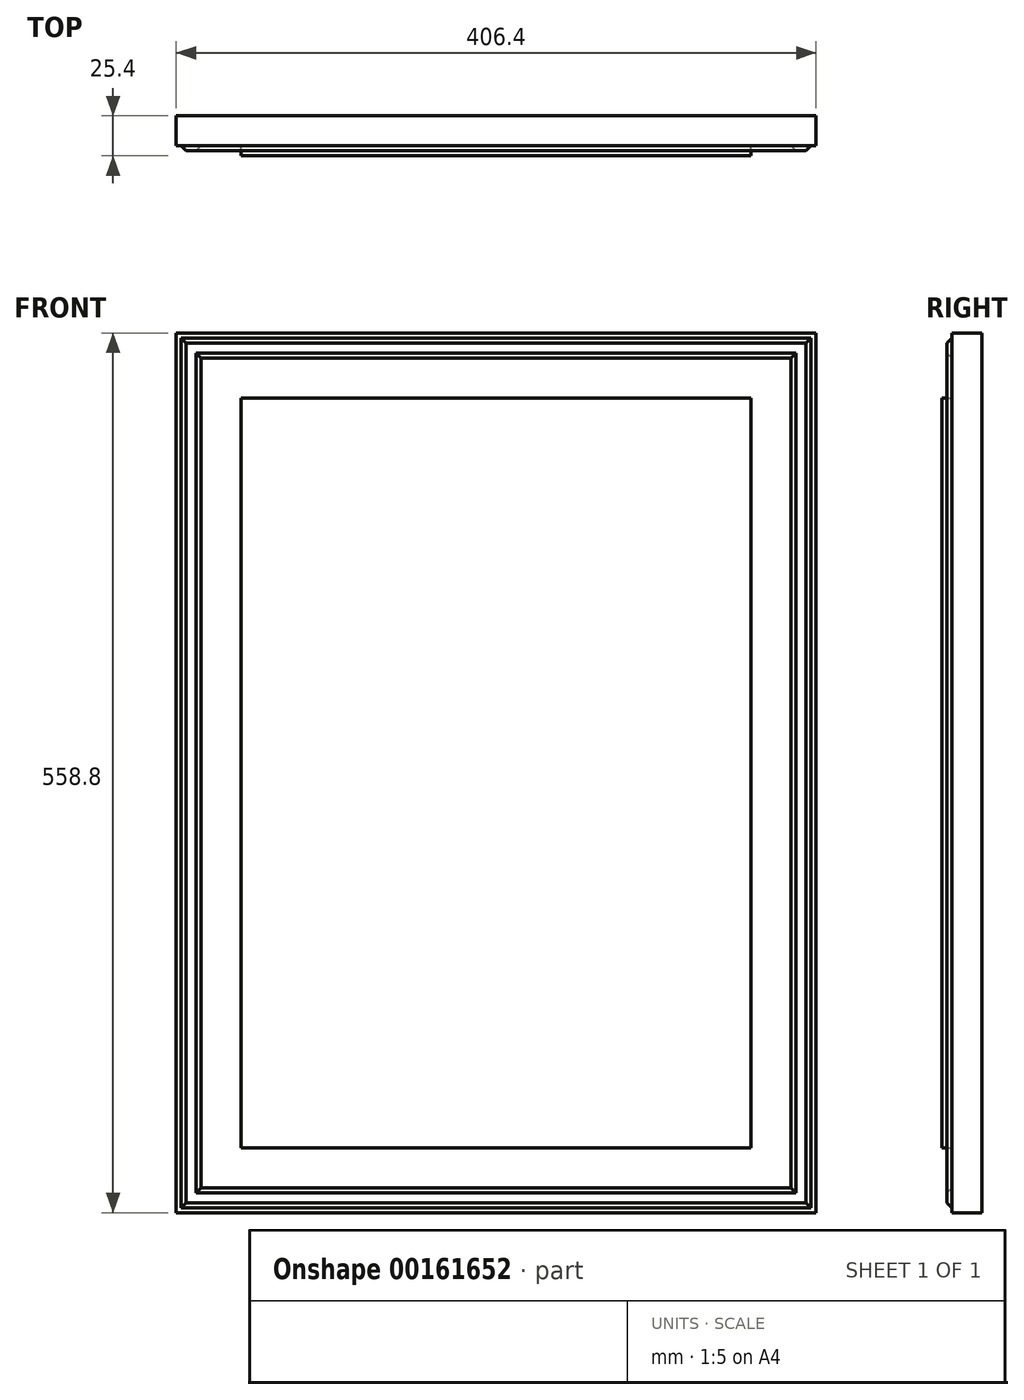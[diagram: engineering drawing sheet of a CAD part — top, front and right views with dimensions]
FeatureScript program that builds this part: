
annotation { "Feature Type Name" : "Feature", "Feature Type Description" : "" }
export const myFeature = defineFeature(function(context is Context, id is Id, definition is map)
    precondition{}
    {
        {
            var Q0;
            Q0=qCreatedBy(makeId("Front.planeOp"),FACE);
            var sketch = newSketch(context, id + "F0", { "sketchPlane" : qUnion([Q0])});
            skLineSegment(sketch, "E0.bottom", {"start": v(203.2, -279.4) * mm, "end": v(0, -279.4) * mm});
            skLineSegment(sketch, "E0.top", {"start": v(203.2, 279.4) * mm, "end": v(0, 279.4) * mm});
            skLineSegment(sketch, "E0.left", {"start": v(203.2, -279.4) * mm, "end": v(203.2, 279.4) * mm});
            skLineSegment(sketch, "E0.right", {"start": v(0, -279.4) * mm, "end": v(0, 279.4) * mm});
            skPoint(sketch, "E0.middle", {"position": v(101.6, 0) * mm});
            skSolve(sketch);
        }
        {
            var Q0;
            Q0 = qSketchRegion(id + "F0", true);
            extrude(context, id + "F1", {"entities" : qUnion([Q0]), "depth" : 25.4 * mm});
        }
        {
            var Q0;
            Q0=qCreatedBy(makeId("Right.planeOp"),FACE);
            var sketch = newSketch(context, id + "F2", { "sketchPlane" : qUnion([Q0])});
            skLineSegment(sketch, "E1", {"start": v(-19.05, -238.13) * mm, "end": v(-19.05, -263.53) * mm});
            skLineSegment(sketch, "E2", {"start": v(-19.05, -263.53) * mm, "end": v(-22.23, -266.7) * mm});
            skLineSegment(sketch, "E3", {"start": v(-22.23, -266.7) * mm, "end": v(-22.23, -273.05) * mm});
            skLineSegment(sketch, "E4", {"start": v(-22.22, -273.05) * mm, "end": v(-19.05, -276.23) * mm});
            skLineSegment(sketch, "E5", {"start": v(-19.05, -276.23) * mm, "end": v(-19.05, -279.4) * mm});
            skLineSegment(sketch, "E6", {"start": v(-19.05, -279.4) * mm, "end": v(-25.4, -279.4) * mm});
            skLineSegment(sketch, "E7", {"start": v(-25.4, -279.4) * mm, "end": v(-25.4, -238.13) * mm});
            skLineSegment(sketch, "E8", {"start": v(-25.4, -238.13) * mm, "end": v(-19.05, -238.13) * mm});
            skSolve(sketch);
        }
        {
            var Q0;
            Q0=makeQuery(id+"F1.opExtrude","CAP_FACE",FACE,{"disambiguationData":[OSD([sQuery(id+"F0.wireOp",EDGE,"E0.bottom"),sQuery(id+"F0.wireOp",EDGE,"E0.top"),sQuery(id+"F0.wireOp",EDGE,"E0.left"),sQuery(id+"F0.wireOp",EDGE,"E0.right")])],"isStart":false});
            var sketch = newSketch(context, id + "F3", { "sketchPlane" : qUnion([Q0])});
            skLineSegment(sketch, "E9", {"start": v(0, -238.13) * mm, "end": v(161.93, -238.13) * mm});
            skLineSegment(sketch, "E10", {"start": v(161.93, -238.13) * mm, "end": v(161.93, 238.13) * mm});
            skLineSegment(sketch, "E11", {"start": v(161.92, 238.13) * mm, "end": v(0, 238.13) * mm});
            skLineSegment(sketch, "E12", {"start": v(0, -238.13) * mm, "end": v(0, 238.13) * mm, "construction": true});
            skLineSegment(sketch, "E13", {"start": v(0, 238.13) * mm, "end": v(0, 279.4) * mm, "construction": true});
            skPoint(sketch, "E14.endSnap0", {"position": v(161.93, 0) * mm});
            skLineSegment(sketch, "E15", {"start": v(203.2, 0) * mm, "end": v(161.93, 0) * mm, "construction": true});
            skSolve(sketch);
        }
        {
            var Q0;
            Q0 = qSketchRegion(id + "F2", true);
            var Q1;
            Q1 = qConstructionFilter(qBodyType(qCreatedBy(id + "F3" ,EDGE), BodyType.WIRE), ConstructionObject.NO);
            sweep(context, id + "F4", {"operationType" : NewBodyOperationType.REMOVE, "profiles" : qUnion([Q0]), "path" : qUnion([Q1])});
        }
        {
            var Q0;
            Q0=makeQuery(id+"F1.opExtrude","SWEPT_BODY",BODY,{"disambiguationData":[OSD([sQuery(id+"F0.wireOp",EDGE,"E0.bottom"),sQuery(id+"F0.wireOp",EDGE,"E0.top"),sQuery(id+"F0.wireOp",EDGE,"E0.left"),sQuery(id+"F0.wireOp",EDGE,"E0.right")])]});
            var Q1;
            Q1=qCreatedBy(makeId("Right.planeOp"),FACE);
            mirror(context, id + "F5", {"operationType" : NewBodyOperationType.ADD, "entities" : qUnion([Q0]), "mirrorPlane" : qUnion([Q1])});
        }
    });
